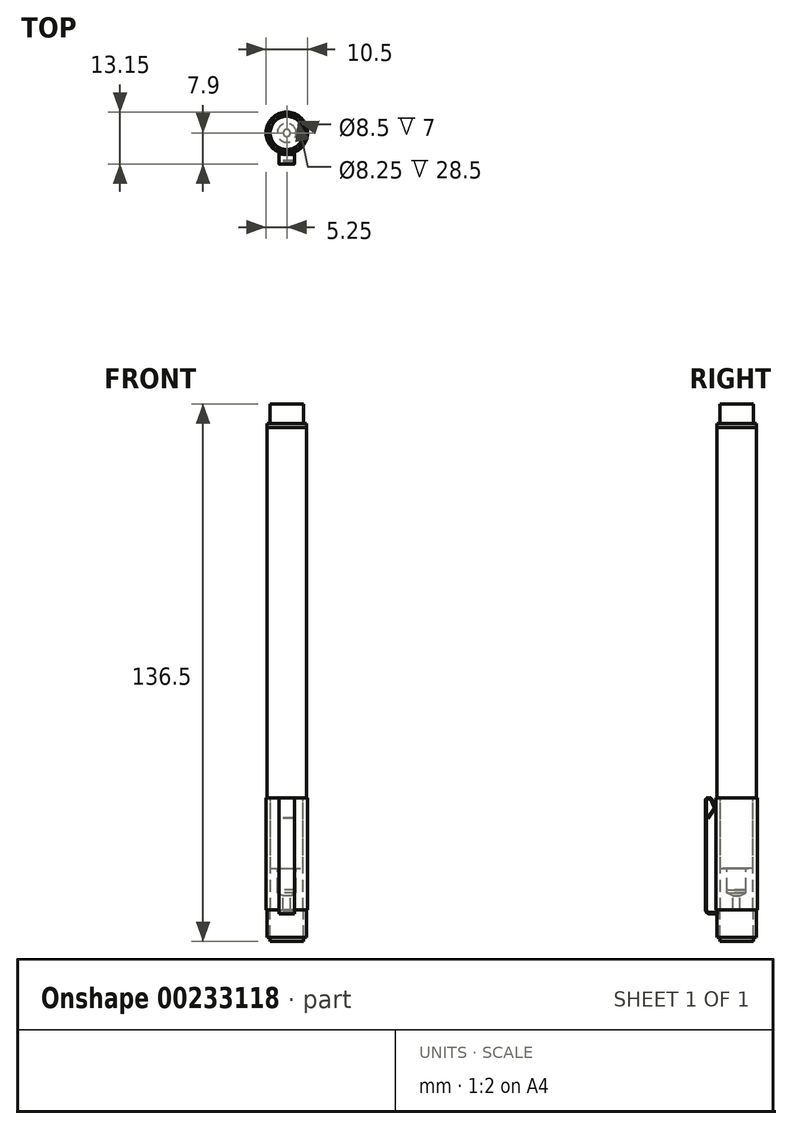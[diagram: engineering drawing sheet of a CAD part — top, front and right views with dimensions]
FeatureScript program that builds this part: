
annotation { "Feature Type Name" : "Feature", "Feature Type Description" : "" }
export const myFeature = defineFeature(function(context is Context, id is Id, definition is map)
    precondition{}
    {
        {
            var Q0;
            Q0=qCreatedBy(makeId("Top.planeOp"),FACE);
            var sketch = newSketch(context, id + "F0", { "sketchPlane" : qUnion([Q0])});
            skCircle(sketch, "E0", {"center": v(0, 0) * mm, "radius": 5 * mm});
            skSolve(sketch);
        }
        {
            var Q0;
            Q0 = qSketchRegion(id + "F0", true);
            extrude(context, id + "F1", {"entities" : qUnion([Q0]), "depth" : 94 * mm});
        }
        {
            var Q0;
            Q0=makeQuery(id+"F1.opExtrude","CAP_FACE",FACE,{"disambiguationData":[OSD([sQuery(id+"F0.wireOp",EDGE,"E0")])],"isStart":false});
            var sketch = newSketch(context, id + "F2", { "sketchPlane" : qUnion([Q0])});
            skCircle(sketch, "E1", {"center": v(0, 0) * mm, "radius": 5 * mm});
            skSolve(sketch);
        }
        {
            var Q0;
            Q0 = qSketchRegion(id + "F2", true);
            extrude(context, id + "F3", {"entities" : qUnion([Q0]), "depth" : 1 * mm});
        }
        {
            var Q0;
            Q0=makeQuery(id+"F1.opExtrude","CAP_FACE",FACE,{"disambiguationData":[OSD([sQuery(id+"F0.wireOp",EDGE,"E0")])],"isStart":true});
            var sketch = newSketch(context, id + "F4", { "sketchPlane" : qUnion([Q0])});
            skCircle(sketch, "E2", {"center": v(0, 0) * mm, "radius": 4.12 * mm});
            skSolve(sketch);
        }
        {
            var Q0;
            Q0 = qSketchRegion(id + "F4", true);
            extrude(context, id + "F5", {"entities" : qUnion([Q0]), "operationType" : NewBodyOperationType.ADD, "depth" : 18 * mm});
        }
        {
            var Q0;
            Q0=makeQuery(id+"F5.opExtrude","CAP_FACE",FACE,{"disambiguationData":[OSD([sQuery(id+"F4.wireOp",EDGE,"E2")])],"isStart":false});
            var sketch = newSketch(context, id + "F6", { "sketchPlane" : qUnion([Q0])});
            skCircle(sketch, "E3", {"center": v(0, 0) * mm, "radius": 2.4 * mm});
            skSolve(sketch);
        }
        {
            var Q0;
            Q0 = qSketchRegion(id + "F6", true);
            extrude(context, id + "F7", {"entities" : qUnion([Q0]), "operationType" : NewBodyOperationType.ADD, "depth" : 5.4 * mm});
        }
        {
            var Q0;
            Q0=qCreatedBy(makeId("Front.planeOp"),FACE);
            var sketch = newSketch(context, id + "F8", { "sketchPlane" : qUnion([Q0])});
            skLineSegment(sketch, "E4", {"start": v(2.4, -23.4) * mm, "end": v(2.4, -24.15) * mm});
            skLineSegment(sketch, "E5", {"start": v(2.4, -24.15) * mm, "end": v(0.9, -24.9) * mm});
            skLineSegment(sketch, "E6", {"start": v(0.9, -24.9) * mm, "end": v(0.9, -28.9) * mm});
            skLineSegment(sketch, "E7", {"start": v(0.9, -28.9) * mm, "end": v(0, -28.9) * mm});
            skLineSegment(sketch, "E8", {"start": v(2.4, -23.4) * mm, "end": v(0, -23.4) * mm});
            skLineSegment(sketch, "E9", {"start": v(0, -23.4) * mm, "end": v(0, -28.9) * mm});
            skSolve(sketch);
        }
        {
            var Q0;
            Q0=makeQuery(id+"F8.imprint","IMPRINT",FACE,{"disambiguationData":[TD([[makeQuery(id+"F8.imprint","IMPRINT",EDGE,{"derivedFrom":sQuery(id+"F8.wireOp",EDGE,"E4")}),-1.0]])]});
            var Q1;
            Q1=sQuery(id+"F8.wireOp",EDGE,"E9");
            revolve(context, id + "F9", {"entities" : qUnion([Q0]), "axis" : qUnion([Q1]), "revolveType" : RevolveType.FULL});
        }
        {
            var Q0;
            Q0=makeQuery(id+"F3.opExtrude","CAP_FACE",FACE,{"disambiguationData":[OSD([sQuery(id+"F2.wireOp",EDGE,"E1")])],"isStart":false});
            var sketch = newSketch(context, id + "F10", { "sketchPlane" : qUnion([Q0])});
            skCircle(sketch, "E10", {"center": v(0, 0) * mm, "radius": 4.25 * mm});
            skSolve(sketch);
        }
        {
            var Q0;
            Q0 = qSketchRegion(id + "F10", true);
            extrude(context, id + "F11", {"entities" : qUnion([Q0]), "operationType" : NewBodyOperationType.ADD, "depth" : 5 * mm});
        }
        {
            var Q0;
            Q0=qCreatedBy(makeId("Front.planeOp"),FACE);
            var sketch = newSketch(context, id + "F12", { "sketchPlane" : qUnion([Q0])});
            skLineSegment(sketch, "E11", {"start": v(0, -28.9) * mm, "end": v(0.6, -28.9) * mm});
            skLineSegment(sketch, "E12", {"start": v(0.6, -28.9) * mm, "end": v(0.6, -30.31) * mm});
            skLineSegment(sketch, "E13", {"start": v(0.6, -30.31) * mm, "end": v(0, -30.5) * mm});
            skLineSegment(sketch, "E14", {"start": v(0, -30.5) * mm, "end": v(0, -28.9) * mm});
            skSolve(sketch);
        }
        {
            var Q0;
            Q0=makeQuery(id+"F12.imprint","IMPRINT",FACE,{"disambiguationData":[TD([[makeQuery(id+"F12.imprint","IMPRINT",EDGE,{"derivedFrom":sQuery(id+"F12.wireOp",EDGE,"E11")}),-1.0]])]});
            var Q1;
            Q1=sQuery(id+"F12.wireOp",EDGE,"E14");
            revolve(context, id + "F13", {"entities" : qUnion([Q0]), "axis" : qUnion([Q1]), "revolveType" : RevolveType.FULL});
        }
        {
            var Q0;
            Q0=makeQuery(id+"F1.opExtrude","CAP_FACE",FACE,{"disambiguationData":[OSD([sQuery(id+"F0.wireOp",EDGE,"E0")])],"isStart":true});
            var sketch = newSketch(context, id + "F14", { "sketchPlane" : qUnion([Q0])});
            skCircle(sketch, "E15", {"center": v(0, 0) * mm, "radius": 5.25 * mm});
            skCircle(sketch, "E16.0", {"center": v(0, 0) * mm, "radius": 4.12 * mm});
            skSolve(sketch);
        }
        {
            var Q0;
            Q0 = qSketchRegion(id + "F14", true);
            extrude(context, id + "F15", {"entities" : qUnion([Q0]), "depth" : 28.5 * mm});
        }
        {
            var Q0;
            Q0=makeQuery(id+"F15.opExtrude","CAP_FACE",FACE,{"disambiguationData":[OSD([sQuery(id+"F14.wireOp",EDGE,"E15"),sQuery(id+"F14.wireOp",EDGE,"E16.0")])],"isStart":false});
            var sketch = newSketch(context, id + "F16", { "sketchPlane" : qUnion([Q0])});
            skCircle(sketch, "E17", {"center": v(0, 0) * mm, "radius": 4.25 * mm});
            skSolve(sketch);
        }
        {
            var Q0;
            Q0 = qSketchRegion(id + "F16", true);
            extrude(context, id + "F17", {"entities" : qUnion([Q0]), "operationType" : NewBodyOperationType.ADD, "depth" : (36.5 - 28.5) * mm});
        }
        {
            var Q0;
            Q0=makeQuery(id+"F15.opExtrude","CAP_FACE",FACE,{"disambiguationData":[OSD([sQuery(id+"F14.wireOp",EDGE,"E15"),sQuery(id+"F14.wireOp",EDGE,"E16.0")])],"isStart":false});
            var sketch = newSketch(context, id + "F18", { "sketchPlane" : qUnion([Q0])});
            skCircle(sketch, "E18.0", {"center": v(0, 0) * mm, "radius": 4.25 * mm});
            skCircle(sketch, "E19", {"center": v(0, 0) * mm, "radius": 5 * mm});
            skSolve(sketch);
        }
        {
            var Q0;
            Q0 = qSketchRegion(id + "F18", true);
            extrude(context, id + "F19", {"entities" : qUnion([Q0]), "depth" : 7 * mm});
        }
        {
            var Q0;
            Q0=qCreatedBy(makeId("Right.planeOp"),FACE);
            var sketch = newSketch(context, id + "F20", { "sketchPlane" : qUnion([Q0])});
            skLineSegment(sketch, "E20", {"start": v(-7.08, -5.3) * mm, "end": v(-5.54, -2.89) * mm});
            skLineSegment(sketch, "E21", {"start": v(-5.5, -2.24) * mm, "end": v(-6.27, -0.42) * mm});
            skLineSegment(sketch, "E22", {"start": v(-6.91, 0) * mm, "end": v(-7.2, 0) * mm});
            skLineSegment(sketch, "E23", {"start": v(-7.9, -0.7) * mm, "end": v(-7.9, -28.5) * mm});
            skLineSegment(sketch, "E24", {"start": v(-6.9, -29.5) * mm, "end": v(-4.8, -29.5) * mm});
            skPoint(sketch, "E25.visualSharp", {"position": v(-7.9, 0) * mm});
            skArc(sketch, "E25.filletArc", {"start": v(-7.2, 0) * mm, "mid": v(-7.7, -0.2) * mm, "end": v(-7.9, -0.7) * mm});
            skPoint(sketch, "E26.visualSharp", {"position": v(-6.45, 0) * mm});
            skArc(sketch, "E26.filletArc", {"start": v(-6.27, -0.42) * mm, "mid": v(-6.53, -0.12) * mm, "end": v(-6.91, 0) * mm});
            skPoint(sketch, "E27.visualSharp", {"position": v(-5.34, -2.58) * mm});
            skArc(sketch, "E27.filletArc", {"start": v(-5.54, -2.89) * mm, "mid": v(-5.44, -2.57) * mm, "end": v(-5.5, -2.24) * mm});
            skPoint(sketch, "E28.visualSharp", {"position": v(-7.9, -29.5) * mm});
            skArc(sketch, "E28.filletArc", {"start": v(-7.9, -28.5) * mm, "mid": v(-7.6, -29.2) * mm, "end": v(-6.9, -29.5) * mm});
            skLineSegment(sketch, "E29.0", {"start": v(-6.9, -29.2) * mm, "end": v(-4.8, -29.2) * mm});
            skArc(sketch, "E29.1", {"start": v(-7.6, -28.5) * mm, "mid": v(-7.4, -29) * mm, "end": v(-6.9, -29.2) * mm});
            skLineSegment(sketch, "E29.2", {"start": v(-7.6, -0.7) * mm, "end": v(-7.6, -28.5) * mm});
            skArc(sketch, "E29.3", {"start": v(-7.2, -0.3) * mm, "mid": v(-7.48, -0.42) * mm, "end": v(-7.6, -0.7) * mm});
            skLineSegment(sketch, "E29.4", {"start": v(-6.91, -0.3) * mm, "end": v(-7.2, -0.3) * mm});
            skLineSegment(sketch, "E29.5", {"start": v(-7.33, -5.13) * mm, "end": v(-5.8, -2.73) * mm});
            skArc(sketch, "E29.6", {"start": v(-5.8, -2.73) * mm, "mid": v(-5.73, -2.55) * mm, "end": v(-5.77, -2.35) * mm});
            skLineSegment(sketch, "E29.7", {"start": v(-5.77, -2.35) * mm, "end": v(-6.55, -0.54) * mm});
            skArc(sketch, "E29.8", {"start": v(-6.55, -0.54) * mm, "mid": v(-6.7, -0.37) * mm, "end": v(-6.91, -0.3) * mm});
            skLineSegment(sketch, "E30", {"start": v(-7.33, -5.13) * mm, "end": v(-7.08, -5.3) * mm});
            skLineSegment(sketch, "E31", {"start": v(-4.8, -29.2) * mm, "end": v(-4.8, -29.5) * mm});
            skSolve(sketch);
        }
        {
            var Q0;
            Q0 = qSketchRegion(id + "F20", true);
            extrude(context, id + "F21", {"entities" : qUnion([Q0]), "operationType" : NewBodyOperationType.ADD, "depth" : 4 * mm, "symmetric" : true});
        }
    });
